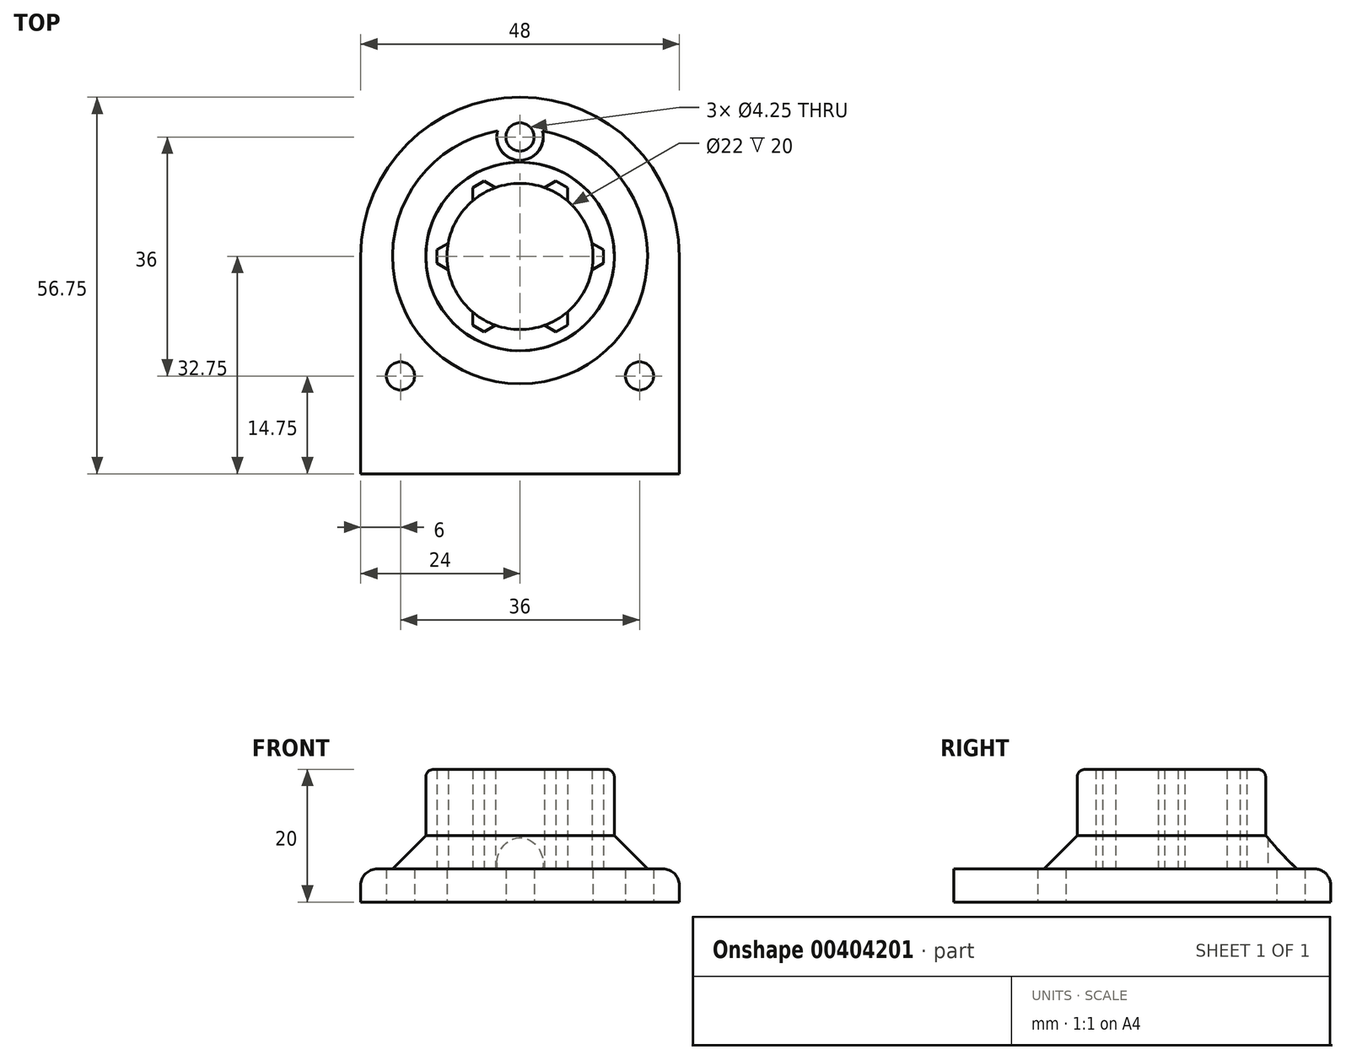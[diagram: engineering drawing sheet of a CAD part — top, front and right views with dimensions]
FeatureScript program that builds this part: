
annotation { "Feature Type Name" : "Feature", "Feature Type Description" : "" }
export const myFeature = defineFeature(function(context is Context, id is Id, definition is map)
    precondition{}
    {
        {
            var Q0;
            Q0=qCreatedBy(makeId("Top.planeOp"),FACE);
            var sketch = newSketch(context, id + "F0", { "sketchPlane" : qUnion([Q0])});
            skCircle(sketch, "E0", {"center": v(0, 0) * mm, "radius": 11 * mm});
            skArc(sketch, "E1", {"start": v(24, 0) * mm, "mid": v(0, 24) * mm, "end": v(-24, 0) * mm});
            skLineSegment(sketch, "E2", {"start": v(-24, 0) * mm, "end": v(-24, -32.75) * mm});
            skLineSegment(sketch, "E3", {"start": v(-24, -32.75) * mm, "end": v(0, -32.75) * mm});
            skLineSegment(sketch, "E4", {"start": v(0, -32.75) * mm, "end": v(24, -32.75) * mm});
            skLineSegment(sketch, "E5", {"start": v(24, -32.75) * mm, "end": v(24, 0) * mm});
            skCircle(sketch, "E6", {"center": v(-18, -18) * mm, "radius": 2.12 * mm});
            skCircle(sketch, "E7.MirrorC", {"center": v(18, -18) * mm, "radius": 2.12 * mm});
            skCircle(sketch, "E8", {"center": v(0, 18) * mm, "radius": 2.12 * mm});
            skSolve(sketch);
        }
        {
            var Q0;
            Q0 = qSketchRegion(id + "F0", true);
            extrude(context, id + "F1", {"entities" : qUnion([Q0]), "depth" : 5 * mm});
        }
        {
            var Q0;
            Q0=makeQuery(id+"F1.opExtrude","CAP_FACE",FACE,{"disambiguationData":[OSD([sQuery(id+"F0.wireOp",EDGE,"E0"),sQuery(id+"F0.wireOp",EDGE,"E1"),sQuery(id+"F0.wireOp",EDGE,"E2"),sQuery(id+"F0.wireOp",EDGE,"E3"),sQuery(id+"F0.wireOp",EDGE,"E4"),sQuery(id+"F0.wireOp",EDGE,"E5"),sQuery(id+"F0.wireOp",EDGE,"E6"),sQuery(id+"F0.wireOp",EDGE,"E7.MirrorC"),sQuery(id+"F0.wireOp",EDGE,"E8")])],"isStart":false});
            var sketch = newSketch(context, id + "F2", { "sketchPlane" : qUnion([Q0])});
            skArc(sketch, "E9", {"start": v(10.86, 1.73) * mm, "mid": v(9.6, 5.38) * mm, "end": v(7.14, 8.37) * mm});
            skCircle(sketch, "E10", {"center": v(0, 0) * mm, "radius": 14.2 * mm});
            skCircle(sketch, "E11.cCircle", {"center": v(10.82, 0) * mm, "radius": 1.73 * mm, "construction": true});
            skLineSegment(sketch, "E11.0", {"start": v(12.55, 1) * mm, "end": v(12.55, -1) * mm});
            skLineSegment(sketch, "E11.1", {"start": v(12.55, -1) * mm, "end": v(10.82, -2) * mm});
            skLineSegment(sketch, "E11.2", {"start": v(10.82, -2) * mm, "end": v(9.08, -1) * mm, "construction": true});
            skLineSegment(sketch, "E11.3", {"start": v(9.08, -1) * mm, "end": v(9.08, 1) * mm, "construction": true});
            skLineSegment(sketch, "E11.4", {"start": v(9.08, 1) * mm, "end": v(10.82, 2) * mm, "construction": true});
            skLineSegment(sketch, "E11.5", {"start": v(10.82, 2) * mm, "end": v(12.55, 1) * mm});
            skPoint(sketch, "E11.0.midPoint", {"position": v(12.55, 0) * mm});
            skLineSegment(sketch, "E12.1.0", {"start": v(3.68, 10.37) * mm, "end": v(5.4, 11.37) * mm});
            skLineSegment(sketch, "E12.1.1", {"start": v(5.4, 11.37) * mm, "end": v(7.14, 10.37) * mm});
            skLineSegment(sketch, "E12.1.2", {"start": v(7.14, 10.37) * mm, "end": v(7.14, 8.37) * mm});
            skLineSegment(sketch, "E12.2.0", {"start": v(-7.14, 8.37) * mm, "end": v(-7.14, 10.37) * mm});
            skLineSegment(sketch, "E12.2.1", {"start": v(-7.14, 10.37) * mm, "end": v(-5.4, 11.37) * mm});
            skLineSegment(sketch, "E12.2.2", {"start": v(-5.4, 11.37) * mm, "end": v(-3.68, 10.37) * mm});
            skLineSegment(sketch, "E12.3.0", {"start": v(-10.82, -2) * mm, "end": v(-12.55, -1) * mm});
            skLineSegment(sketch, "E12.3.1", {"start": v(-12.55, -1) * mm, "end": v(-12.55, 1) * mm});
            skLineSegment(sketch, "E12.3.2", {"start": v(-12.55, 1) * mm, "end": v(-10.82, 2) * mm});
            skLineSegment(sketch, "E12.4.0", {"start": v(-3.68, -10.37) * mm, "end": v(-5.4, -11.37) * mm});
            skLineSegment(sketch, "E12.4.1", {"start": v(-5.4, -11.37) * mm, "end": v(-7.14, -10.37) * mm});
            skLineSegment(sketch, "E12.4.2", {"start": v(-7.14, -10.37) * mm, "end": v(-7.14, -8.37) * mm});
            skLineSegment(sketch, "E12.5.0", {"start": v(7.14, -8.37) * mm, "end": v(7.14, -10.37) * mm});
            skLineSegment(sketch, "E12.5.1", {"start": v(7.14, -10.37) * mm, "end": v(5.4, -11.37) * mm});
            skLineSegment(sketch, "E12.5.2", {"start": v(5.4, -11.37) * mm, "end": v(3.68, -10.37) * mm});
            skArc(sketch, "E13.trimOffspring", {"start": v(3.68, 10.37) * mm, "mid": v(0, 11) * mm, "end": v(-3.68, 10.37) * mm});
            skArc(sketch, "E14.trimOffspring", {"start": v(-7.14, 8.37) * mm, "mid": v(-9.53, 5.5) * mm, "end": v(-10.82, 2) * mm});
            skArc(sketch, "E15.trimOffspring", {"start": v(-10.82, -2) * mm, "mid": v(-9.53, -5.5) * mm, "end": v(-7.14, -8.37) * mm});
            skArc(sketch, "E16.trimOffspring", {"start": v(7.14, -8.37) * mm, "mid": v(9.6, -5.38) * mm, "end": v(10.86, -1.73) * mm});
            skArc(sketch, "E17.trimOffspring", {"start": v(-3.68, -10.37) * mm, "mid": v(0, -11) * mm, "end": v(3.68, -10.37) * mm});
            skSolve(sketch);
        }
        {
            var Q0;
            Q0 = qSketchRegion(id + "F2", true);
            extrude(context, id + "F3", {"entities" : qUnion([Q0]), "operationType" : NewBodyOperationType.ADD, "depth" : 15 * mm});
        }
        {
            var Q0;
            Q0=makeQuery(id+"F3.opExtrude","CAP_EDGE",EDGE,{"disambiguationData":[OSD([sQuery(id+"F2.wireOp",EDGE,"E10")])],"isStart":true});
            chamfer(context, id + "F4", {"entities" : qUnion([Q0]), "width" : 5 * mm, "tangentPropagation" : true});
        }
        {
            var Q0;
            Q0=makeQuery(id+"F3.opExtrude","CAP_EDGE",EDGE,{"disambiguationData":[OSD([sQuery(id+"F2.wireOp",EDGE,"E10")])],"isStart":false});
            fillet(context, id + "F5", {"entities" : qUnion([Q0]), "radius" : 1.2 * mm, "tangentPropagation" : true, "allowEdgeOverflow" : false});
        }
        {
            var Q0;
            Q0=makeQuery(id+"F1.opExtrude","CAP_FACE",FACE,{"disambiguationData":[OSD([sQuery(id+"F0.wireOp",EDGE,"E0"),sQuery(id+"F0.wireOp",EDGE,"E1"),sQuery(id+"F0.wireOp",EDGE,"E2"),sQuery(id+"F0.wireOp",EDGE,"E3"),sQuery(id+"F0.wireOp",EDGE,"E4"),sQuery(id+"F0.wireOp",EDGE,"E5"),sQuery(id+"F0.wireOp",EDGE,"E6"),sQuery(id+"F0.wireOp",EDGE,"E7.MirrorC"),sQuery(id+"F0.wireOp",EDGE,"E8")])],"isStart":false});
            var sketch = newSketch(context, id + "F6", { "sketchPlane" : qUnion([Q0])});
            skCircle(sketch, "E18", {"center": v(0, 18) * mm, "radius": 3.5 * mm});
            skSolve(sketch);
        }
        {
            var Q0;
            Q0 = qSketchRegion(id + "F6", true);
            extrude(context, id + "F7", {"entities" : qUnion([Q0]), "operationType" : NewBodyOperationType.REMOVE, "depth" : 25 * mm});
        }
        {
            var Q0;
            Q0=makeQuery(id+"F1.opExtrude","CAP_EDGE",EDGE,{"disambiguationData":[OSD([sQuery(id+"F0.wireOp",EDGE,"E1")])],"isStart":false});
            fillet(context, id + "F8", {"entities" : qUnion([Q0]), "radius" : 2.5 * mm, "tangentPropagation" : true, "allowEdgeOverflow" : false});
        }
    });
